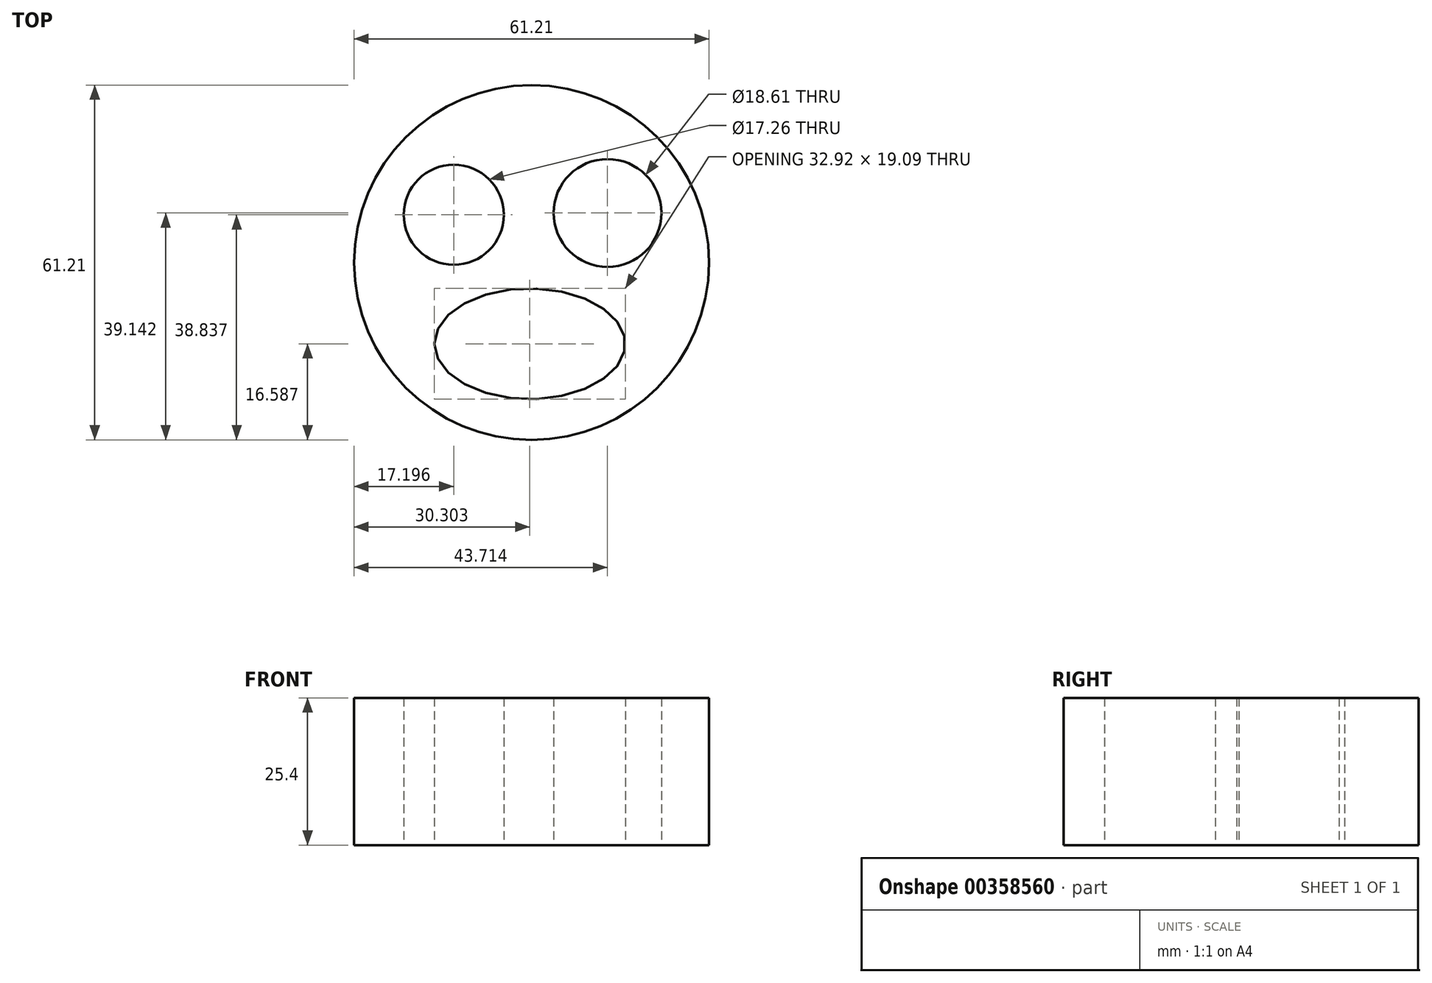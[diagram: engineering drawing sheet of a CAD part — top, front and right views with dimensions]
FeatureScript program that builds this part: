
annotation { "Feature Type Name" : "Feature", "Feature Type Description" : "" }
export const myFeature = defineFeature(function(context is Context, id is Id, definition is map)
    precondition{}
    {
        {
            var Q0;
            Q0=qCreatedBy(makeId("Top.planeOp"),FACE);
            var sketch = newSketch(context, id + "F0", { "sketchPlane" : qUnion([Q0])});
            skPoint(sketch, "E0.end.orphan", {"position": v(0, 53.06) * mm});
            skCircle(sketch, "E1", {"center": v(-40.23, 30.94) * mm, "radius": 8.63 * mm});
            skCircle(sketch, "E2", {"center": v(-13.72, 31.24) * mm, "radius": 9.3 * mm});
            skCircle(sketch, "E3", {"center": v(-26.82, 22.7) * mm, "radius": 30.6 * mm});
            skEllipse(sketch, "E4", {"center": v(-27.13, 8.69) * mm, "majorRadius": 16.46 * mm, "minorRadius": 9.55 * mm, "majorAxis": v(-1, 0)});
            skSolve(sketch);
        }
        {
            var Q0;
            Q0 = qSketchRegion(id + "F0", true);
            extrude(context, id + "F1", {"entities" : qUnion([Q0]), "depth" : 25.4 * mm});
        }
    });
